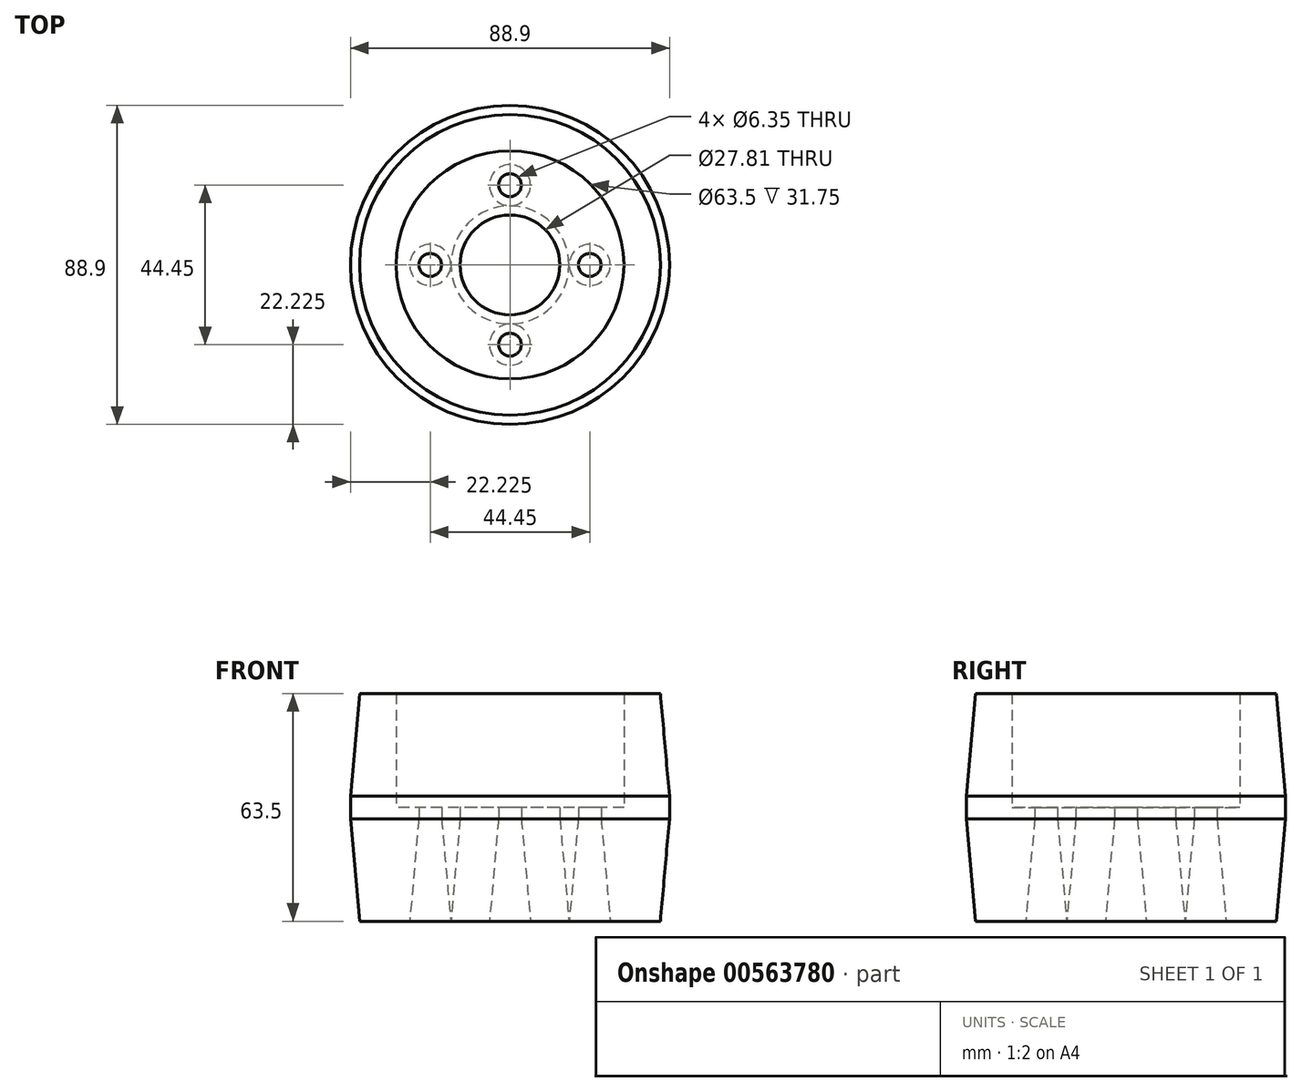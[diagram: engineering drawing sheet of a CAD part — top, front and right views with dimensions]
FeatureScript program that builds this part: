
annotation { "Feature Type Name" : "Feature", "Feature Type Description" : "" }
export const myFeature = defineFeature(function(context is Context, id is Id, definition is map)
    precondition{}
    {
        {
            var Q0;
            Q0=qCreatedBy(makeId("Top.planeOp"),FACE);
            var sketch = newSketch(context, id + "F0", { "sketchPlane" : qUnion([Q0])});
            skCircle(sketch, "E0", {"center": v(0, 0) * mm, "radius": 44.45 * mm});
            skCircle(sketch, "E1", {"center": v(0, 0) * mm, "radius": 31.75 * mm});
            skCircle(sketch, "E2", {"center": v(0, 0) * mm, "radius": 13.9 * mm});
            skCircle(sketch, "E3", {"center": v(0, -22.23) * mm, "radius": 3.18 * mm});
            skCircle(sketch, "E4", {"center": v(22.23, 0) * mm, "radius": 3.18 * mm});
            skCircle(sketch, "E5", {"center": v(0, 22.23) * mm, "radius": 3.18 * mm});
            skCircle(sketch, "E6", {"center": v(-22.23, 0) * mm, "radius": 3.18 * mm});
            skLineSegment(sketch, "E7", {"start": v(-22.23, 0) * mm, "end": v(0, 0) * mm});
            skLineSegment(sketch, "E8", {"start": v(0, 22.23) * mm, "end": v(0, 0) * mm});
            skLineSegment(sketch, "E9", {"start": v(22.23, 0) * mm, "end": v(0, 0) * mm});
            skLineSegment(sketch, "E10", {"start": v(0, -22.23) * mm, "end": v(0, 0) * mm});
            skSolve(sketch);
        }
        {
            var Q0;
            Q0=makeQuery(id+"F0.imprint","IMPRINT",FACE,{"disambiguationData":[TD([[makeQuery(id+"F0.imprint","IMPRINT",EDGE,{"derivedFrom":sQuery(id+"F0.wireOp",EDGE,"E1")}),1.0]])]});
            extrude(context, id + "F1", {"entities" : qUnion([Q0]), "depth" : 31.75 * mm, "offsetDistance" : 25.4 * mm});
        }
        {
            var Q0;
            Q0=makeQuery(id+"F0.imprint","IMPRINT",FACE,{"disambiguationData":[TD([[makeQuery(id+"F0.imprint","IMPRINT",EDGE,{"derivedFrom":sQuery(id+"F0.wireOp",EDGE,"E0")}),1.0]])]});
            extrude(context, id + "F2", {"entities" : qUnion([Q0]), "operationType" : NewBodyOperationType.ADD, "depth" : 63.5 * mm, "offsetDistance" : 25.4 * mm});
        }
        {
            var Q0;
            Q0=makeQuery(id+"F2.opExtrude","CAP_EDGE",EDGE,{"disambiguationData":[OSD([sQuery(id+"F0.wireOp",EDGE,"E0")])],"isStart":false});
            chamfer(context, id + "F3", {"entities" : qUnion([Q0]), "chamferType" : ChamferType.TWO_OFFSETS, "width1" : 2.54 * mm, "oppositeDirection" : false, "width2" : 28.57 * mm, "tangentPropagation" : true});
        }
        {
            var Q0;
            {var subQ0=sQuery(id+"F0.wireOp",EDGE,"E1");Q0=makeQuery(id+"F2.boolean.opBoolean","MERGE",FACE,{"derivedFrom":[makeQuery(id+"F1.opExtrude","CAP_FACE",FACE,{"disambiguationData":[OSD([subQ0,sQuery(id+"F0.wireOp",EDGE,"E2"),sQuery(id+"F0.wireOp",EDGE,"E3"),sQuery(id+"F0.wireOp",EDGE,"E4"),sQuery(id+"F0.wireOp",EDGE,"E5"),sQuery(id+"F0.wireOp",EDGE,"E6")])],"isStart":true}),makeQuery(id+"F2.opExtrude","CAP_FACE",FACE,{"disambiguationData":[OSD([sQuery(id+"F0.wireOp",EDGE,"E0"),subQ0])],"isStart":true})]});}
            chamfer(context, id + "F4", {"entities" : qUnion([Q0]), "chamferType" : ChamferType.TWO_OFFSETS, "width1" : 2.54 * mm, "oppositeDirection" : false, "width2" : 28.57 * mm, "tangentPropagation" : true});
        }
    });
